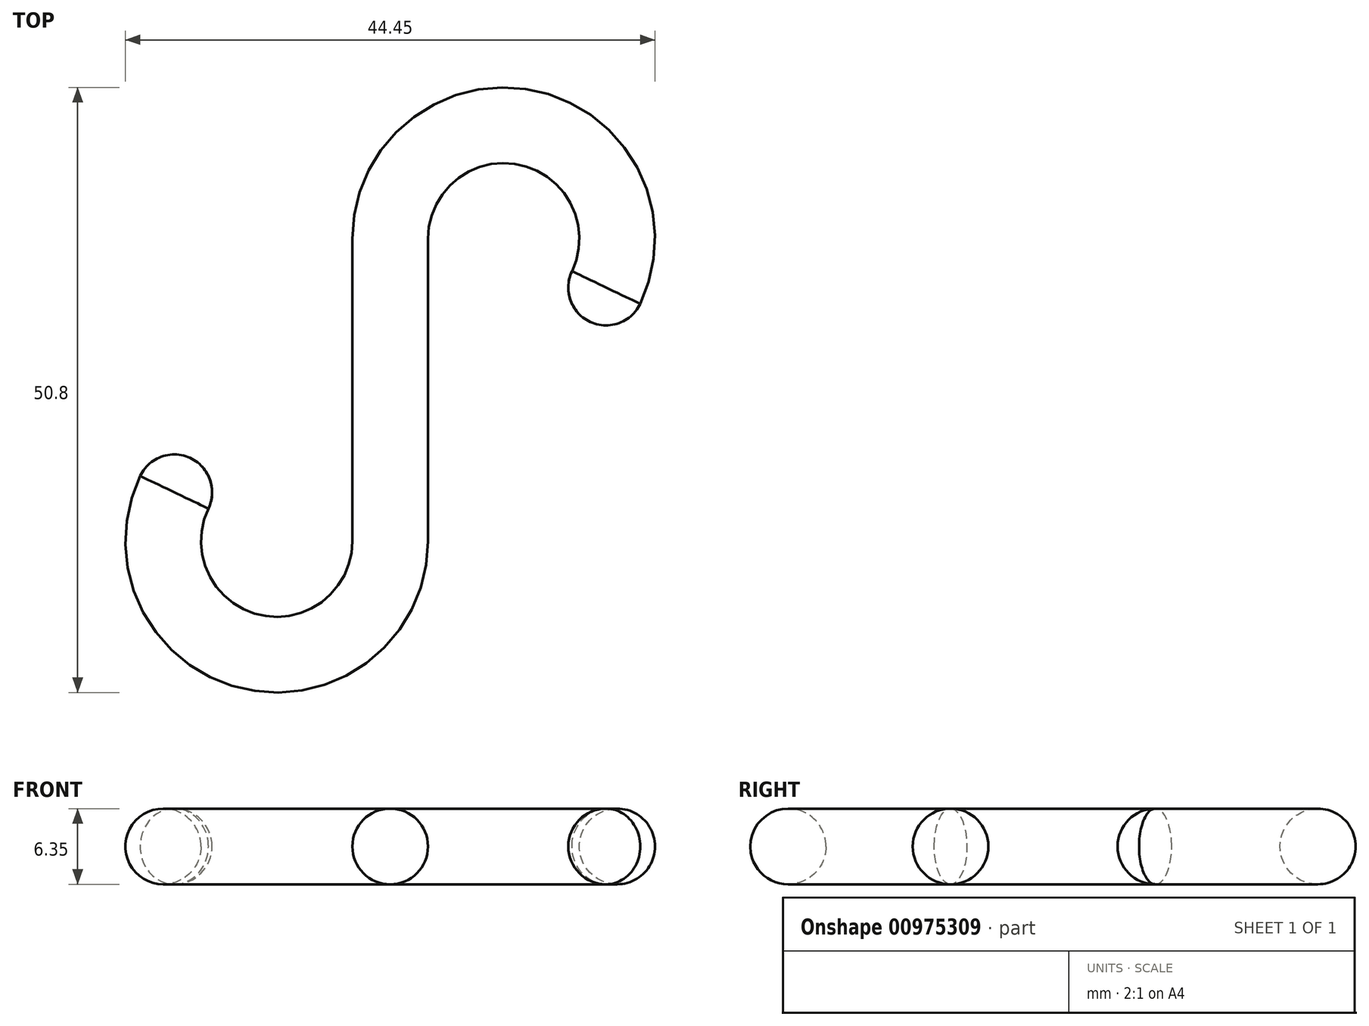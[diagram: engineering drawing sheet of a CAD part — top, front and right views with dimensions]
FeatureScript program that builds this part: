
annotation { "Feature Type Name" : "Feature", "Feature Type Description" : "" }
export const myFeature = defineFeature(function(context is Context, id is Id, definition is map)
    precondition{}
    {
        {
            var Q0;
            Q0=qCreatedBy(makeId("Top.planeOp"),FACE);
            var sketch = newSketch(context, id + "F0", { "sketchPlane" : qUnion([Q0])});
            skLineSegment(sketch, "E0", {"start": v(0, 38.1) * mm, "end": v(0, 12.7) * mm});
            skArc(sketch, "E1", {"start": v(10.84, 33.6) * mm, "mid": v(8.78, 43.97) * mm, "end": v(0, 38.1) * mm});
            skArc(sketch, "E2.0", {"start": v(15.33, 29.12) * mm, "mid": v(11.21, 49.83) * mm, "end": v(-6.35, 38.1) * mm});
            skLineSegment(sketch, "E3", {"start": v(10.84, 33.6) * mm, "end": v(15.33, 29.12) * mm});
            skArc(sketch, "E4", {"start": v(-17.2, 17.2) * mm, "mid": v(-15.13, 6.83) * mm, "end": v(-6.35, 12.7) * mm});
            skArc(sketch, "E5.0", {"start": v(-21.68, 21.68) * mm, "mid": v(-17.56, 0.97) * mm, "end": v(0, 12.7) * mm});
            skPoint(sketch, "E6.end.orphan", {"position": v(-12.7, 0) * mm});
            skPoint(sketch, "E7.orphan", {"position": v(-6.35, 12.7) * mm});
            skLineSegment(sketch, "E8", {"start": v(-17.2, 17.2) * mm, "end": v(-21.68, 21.68) * mm});
            skLineSegment(sketch, "E9", {"start": v(-6.35, 38.1) * mm, "end": v(-6.35, 12.7) * mm});
            skSolve(sketch);
        }
        {
            var Q0;
            Q0=makeQuery(id+"F0.imprint","IMPRINT",FACE,{"disambiguationData":[TD([[makeQuery(id+"F0.imprint","IMPRINT",EDGE,{"derivedFrom":sQuery(id+"F0.wireOp",EDGE,"E0")}),-1.0]])]});
            extrude(context, id + "F1", {"entities" : qUnion([Q0]), "depth" : 6.35 * mm, "offsetDistance" : 25.4 * mm});
        }
        {
            var Q0;
            Q0=makeQuery(id+"F1.opExtrude","CAP_EDGE",EDGE,{"disambiguationData":[OSD([sQuery(id+"F0.wireOp",EDGE,"E2.0")])],"isStart":false});
            var Q1;
            Q1=makeQuery(id+"F1.opExtrude","CAP_EDGE",EDGE,{"disambiguationData":[OSD([sQuery(id+"F0.wireOp",EDGE,"E2.0")])],"isStart":true});
            var Q2;
            Q2=makeQuery(id+"F1.opExtrude","CAP_EDGE",EDGE,{"disambiguationData":[OSD([sQuery(id+"F0.wireOp",EDGE,"E0")])],"isStart":true});
            var Q3;
            Q3=makeQuery(id+"F1.opExtrude","CAP_EDGE",EDGE,{"disambiguationData":[OSD([sQuery(id+"F0.wireOp",EDGE,"E5.0")])],"isStart":false});
            fillet(context, id + "F2", {"entities" : qUnion([Q0, Q1, Q2, Q3]), "radius" : 3.17 * mm, "tangentPropagation" : true, "allowEdgeOverflow" : false});
        }
        {
            var Q0;
            Q0=makeQuery(id+"F2.opFillet","BLEND_EDGE",EDGE,{"blendedFrom":[makeQuery(id+"F1.opExtrude","CAP_EDGE",EDGE,{"disambiguationData":[OSD([sQuery(id+"F0.wireOp",EDGE,"E4")])],"isStart":true}),makeQuery(id+"F1.opExtrude","SWEPT_FACE",FACE,{"disambiguationData":[OSD([sQuery(id+"F0.wireOp",EDGE,"E8")])]})],"blendedInto":[makeQuery(id+"F1.opExtrude","SWEPT_FACE",FACE,{"disambiguationData":[OSD([sQuery(id+"F0.wireOp",EDGE,"E8")])]})]});
            var Q1;
            Q1=makeQuery(id+"F2.opFillet","BLEND_EDGE",EDGE,{"blendedFrom":[makeQuery(id+"F1.opExtrude","CAP_EDGE",EDGE,{"disambiguationData":[OSD([sQuery(id+"F0.wireOp",EDGE,"E1")])],"isStart":true}),makeQuery(id+"F1.opExtrude","SWEPT_FACE",FACE,{"disambiguationData":[OSD([sQuery(id+"F0.wireOp",EDGE,"E3")])]})],"blendedInto":[makeQuery(id+"F1.opExtrude","SWEPT_FACE",FACE,{"disambiguationData":[OSD([sQuery(id+"F0.wireOp",EDGE,"E3")])]})]});
            fillet(context, id + "F3", {"entities" : qUnion([Q0, Q1]), "radius" : 3.17 * mm, "tangentPropagation" : true, "allowEdgeOverflow" : false});
        }
    });
